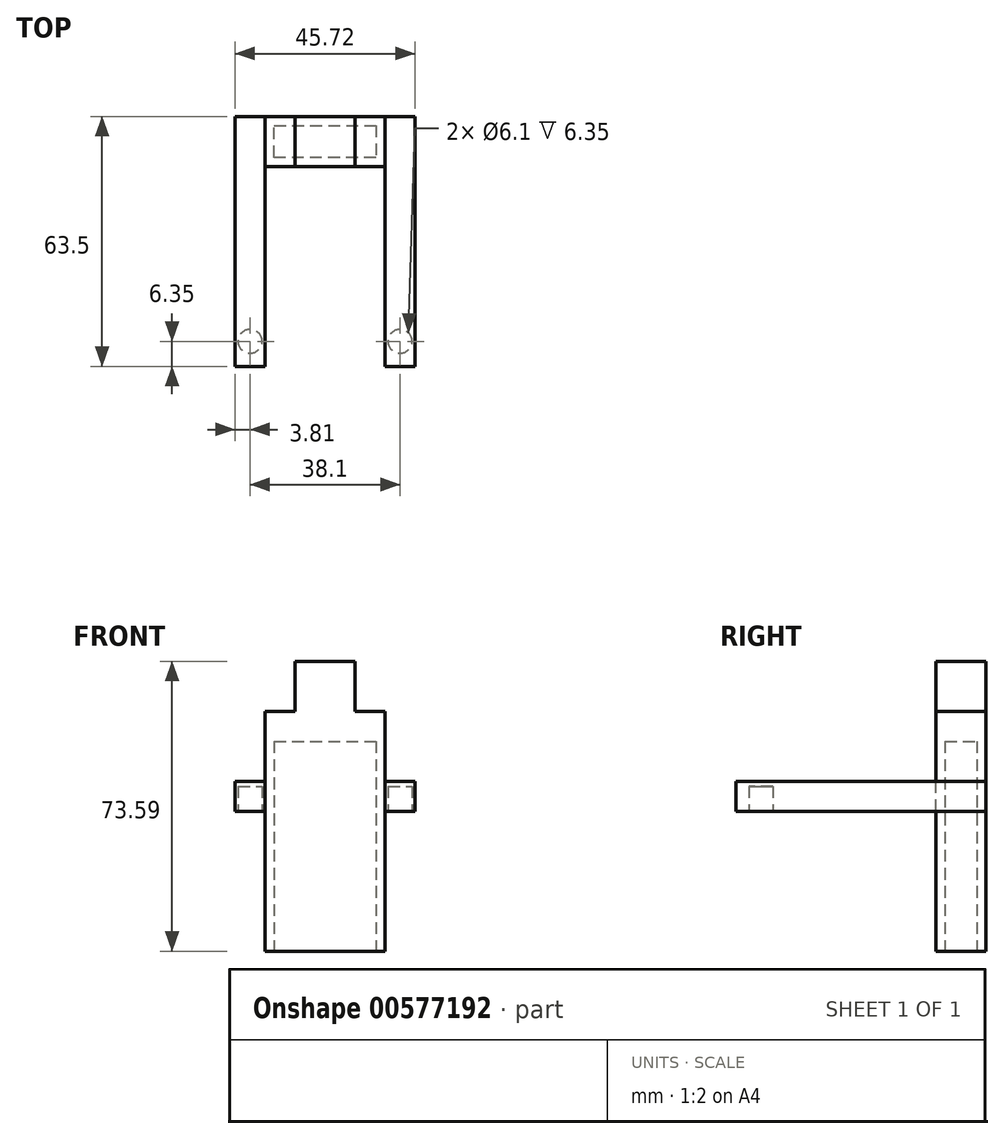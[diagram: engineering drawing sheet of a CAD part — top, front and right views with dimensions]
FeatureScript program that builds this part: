
annotation { "Feature Type Name" : "Feature", "Feature Type Description" : "" }
export const myFeature = defineFeature(function(context is Context, id is Id, definition is map)
    precondition{}
    {
        {
            var Q0;
            Q0=qCreatedBy(makeId("Front.planeOp"),FACE);
            var sketch = newSketch(context, id + "F0", { "sketchPlane" : qUnion([Q0])});
            skLineSegment(sketch, "E0", {"start": v(0, 0) * mm, "end": v(30.48, 0) * mm});
            skLineSegment(sketch, "E1", {"start": v(0, 60.96) * mm, "end": v(0, 0) * mm});
            skLineSegment(sketch, "E2", {"start": v(30.48, 60.96) * mm, "end": v(22.86, 60.96) * mm});
            skLineSegment(sketch, "E3", {"start": v(22.86, 60.96) * mm, "end": v(22.86, 73.59) * mm});
            skLineSegment(sketch, "E4", {"start": v(22.86, 73.59) * mm, "end": v(7.62, 73.59) * mm});
            skLineSegment(sketch, "E5", {"start": v(7.62, 73.59) * mm, "end": v(7.62, 60.96) * mm});
            skLineSegment(sketch, "E6", {"start": v(7.62, 60.96) * mm, "end": v(0, 60.96) * mm});
            skLineSegment(sketch, "E7", {"start": v(30.48, 0) * mm, "end": v(30.48, 60.96) * mm});
            skSolve(sketch);
        }
        {
            var Q0;
            Q0=qCreatedBy(makeId("Front.planeOp"),FACE);
            var sketch = newSketch(context, id + "F1", { "sketchPlane" : qUnion([Q0])});
            skSolve(sketch);
        }
        {
            var Q0;
            Q0 = qSketchRegion(id + "F1", true);
            var Q1;
            Q1=makeQuery(id+"F0.imprint","IMPRINT",FACE,{"disambiguationData":[TD([[makeQuery(id+"F0.imprint","IMPRINT",EDGE,{"derivedFrom":sQuery(id+"F0.wireOp",EDGE,"E0")}),1.0]])]});
            extrude(context, id + "F2", {"entities" : qUnion([Q0, Q1]), "depth" : 12.7 * mm, "offsetDistance" : 25.4 * mm});
        }
        {
            var Q0;
            Q0=qCreatedBy(makeId("Front.planeOp"),FACE);
            var sketch = newSketch(context, id + "F3", { "sketchPlane" : qUnion([Q0])});
            skLineSegment(sketch, "E8", {"start": v(0, 0) * mm, "end": v(0, 35.56) * mm});
            skLineSegment(sketch, "E9", {"start": v(0, 35.56) * mm, "end": v(-7.62, 35.56) * mm});
            skLineSegment(sketch, "E10", {"start": v(-7.62, 35.56) * mm, "end": v(-7.62, 43.18) * mm});
            skLineSegment(sketch, "E11", {"start": v(-7.62, 43.18) * mm, "end": v(0, 43.18) * mm});
            skLineSegment(sketch, "E12", {"start": v(0, 43.18) * mm, "end": v(0, 35.56) * mm});
            skLineSegment(sketch, "E13", {"start": v(30.48, 0) * mm, "end": v(30.48, 35.56) * mm});
            skLineSegment(sketch, "E14", {"start": v(30.48, 35.56) * mm, "end": v(38.1, 35.56) * mm});
            skLineSegment(sketch, "E15", {"start": v(38.1, 35.56) * mm, "end": v(38.1, 43.18) * mm});
            skLineSegment(sketch, "E16", {"start": v(38.1, 43.18) * mm, "end": v(30.48, 43.18) * mm});
            skLineSegment(sketch, "E17", {"start": v(30.48, 43.18) * mm, "end": v(30.48, 35.56) * mm});
            skSolve(sketch);
        }
        {
            var Q0;
            Q0=makeQuery(id+"F3.imprint","IMPRINT",FACE,{"disambiguationData":[TD([[makeQuery(id+"F3.imprint","IMPRINT",EDGE,{"derivedFrom":sQuery(id+"F3.wireOp",EDGE,"E9")}),-1.0]])]});
            var Q1;
            Q1=makeQuery(id+"F3.imprint","IMPRINT",FACE,{"disambiguationData":[TD([[makeQuery(id+"F3.imprint","IMPRINT",EDGE,{"derivedFrom":sQuery(id+"F3.wireOp",EDGE,"E14")}),1.0]])]});
            extrude(context, id + "F4", {"entities" : qUnion([Q0, Q1]), "depth" : 63.5 * mm, "offsetDistance" : 25.4 * mm});
        }
        {
            var Q0;
            Q0=makeQuery(id+"F4.opExtrude","SWEPT_FACE",FACE,{"disambiguationData":[OSD([sQuery(id+"F3.wireOp",EDGE,"E9")])]});
            var sketch = newSketch(context, id + "F5", { "sketchPlane" : qUnion([Q0])});
            skLineSegment(sketch, "E18", {"start": v(-7.62, 31.75) * mm, "end": v(0, 31.75) * mm});
            skLineSegment(sketch, "E19", {"start": v(-3.8, 31.75) * mm, "end": v(-3.8, 57.15) * mm});
            skCircle(sketch, "E20", {"center": v(-3.8, 57.15) * mm, "radius": 3.05 * mm});
            skSolve(sketch);
        }
        {
            var Q0;
            Q0=makeQuery(id+"F4.opExtrude","SWEPT_FACE",FACE,{"disambiguationData":[OSD([sQuery(id+"F3.wireOp",EDGE,"E14")])]});
            var sketch = newSketch(context, id + "F6", { "sketchPlane" : qUnion([Q0])});
            skLineSegment(sketch, "E21", {"start": v(30.48, 31.75) * mm, "end": v(38.1, 31.75) * mm});
            skLineSegment(sketch, "E22", {"start": v(34.3, 31.75) * mm, "end": v(34.3, 57.15) * mm});
            skCircle(sketch, "E23", {"center": v(34.3, 57.15) * mm, "radius": 3.05 * mm});
            skSolve(sketch);
        }
        {
            var Q0;
            Q0=makeQuery(id+"F5.imprint","IMPRINT",FACE,{"disambiguationData":[TD([[makeQuery(id+"F5.imprint","IMPRINT",EDGE,{"derivedFrom":sQuery(id+"F5.wireOp",EDGE,"E20")}),1.0]])]});
            var sketch = newSketch(context, id + "F7", { "sketchPlane" : qUnion([Q0])});
            skSolve(sketch);
        }
        {
            var Q0;
            Q0 = qSketchRegion(id + "F7", true);
            var Q1;
            Q1=makeQuery(id+"F5.imprint","IMPRINT",FACE,{"disambiguationData":[TD([[makeQuery(id+"F5.imprint","IMPRINT",EDGE,{"derivedFrom":sQuery(id+"F5.wireOp",EDGE,"E20")}),1.0]])]});
            extrude(context, id + "F8", {"entities" : qUnion([Q0, Q1]), "operationType" : NewBodyOperationType.REMOVE, "oppositeDirection" : true, "depth" : 6.35 * mm, "offsetDistance" : 25.4 * mm});
        }
        {
            var Q0;
            Q0=makeQuery(id+"F6.imprint","IMPRINT",FACE,{"disambiguationData":[TD([[makeQuery(id+"F6.imprint","IMPRINT",EDGE,{"derivedFrom":sQuery(id+"F6.wireOp",EDGE,"E23")}),1.0]])]});
            var sketch = newSketch(context, id + "F9", { "sketchPlane" : qUnion([Q0])});
            skSolve(sketch);
        }
        {
            var Q0;
            Q0 = qSketchRegion(id + "F9", true);
            var Q1;
            Q1=makeQuery(id+"F6.imprint","IMPRINT",FACE,{"disambiguationData":[TD([[makeQuery(id+"F6.imprint","IMPRINT",EDGE,{"derivedFrom":sQuery(id+"F6.wireOp",EDGE,"E23")}),1.0]])]});
            extrude(context, id + "F10", {"entities" : qUnion([Q0, Q1]), "operationType" : NewBodyOperationType.REMOVE, "oppositeDirection" : true, "depth" : 6.35 * mm, "offsetDistance" : 25.4 * mm});
        }
        {
            var Q0;
            Q0=makeQuery(id+"F2.opExtrude","SWEPT_FACE",FACE,{"disambiguationData":[OSD([sQuery(id+"F0.wireOp",EDGE,"E0")])]});
            var sketch = newSketch(context, id + "F11", { "sketchPlane" : qUnion([Q0])});
            skLineSegment(sketch, "E24.0", {"start": v(2.29, 2.29) * mm, "end": v(28.2, 2.29) * mm});
            skLineSegment(sketch, "E24.1", {"start": v(2.29, 10.41) * mm, "end": v(2.29, 2.29) * mm});
            skLineSegment(sketch, "E24.2", {"start": v(28.2, 10.41) * mm, "end": v(2.29, 10.41) * mm});
            skLineSegment(sketch, "E24.3", {"start": v(28.2, 2.29) * mm, "end": v(28.2, 10.41) * mm});
            skSolve(sketch);
        }
        {
            var Q0;
            Q0=makeQuery(id+"F11.imprint","IMPRINT",FACE,{"disambiguationData":[TD([[makeQuery(id+"F11.imprint","IMPRINT",EDGE,{"derivedFrom":sQuery(id+"F11.wireOp",EDGE,"E24.0")}),1.0]])]});
            extrude(context, id + "F12", {"entities" : qUnion([Q0]), "operationType" : NewBodyOperationType.REMOVE, "oppositeDirection" : true, "depth" : 53.34 * mm, "offsetDistance" : 25.4 * mm});
        }
    });
